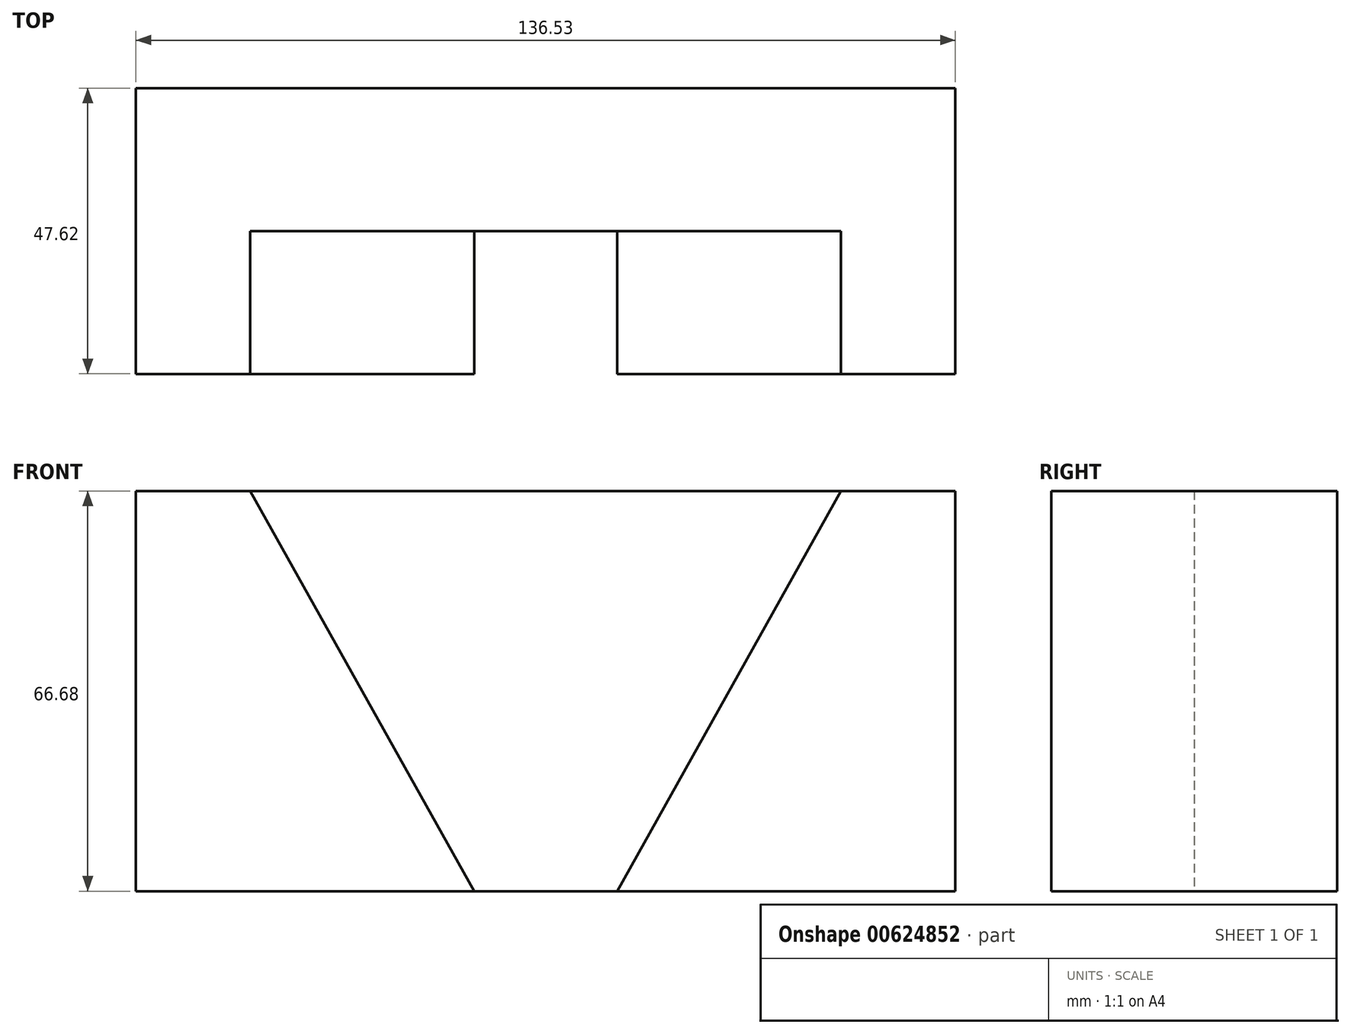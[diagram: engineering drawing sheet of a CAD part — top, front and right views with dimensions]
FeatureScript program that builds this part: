
annotation { "Feature Type Name" : "Feature", "Feature Type Description" : "" }
export const myFeature = defineFeature(function(context is Context, id is Id, definition is map)
    precondition{}
    {
        {
            var Q0;
            Q0=qCreatedBy(makeId("Front.planeOp"),FACE);
            var sketch = newSketch(context, id + "F0", { "sketchPlane" : qUnion([Q0])});
            skLineSegment(sketch, "E0.bottom", {"start": v(17.22, 0) * mm, "end": v(-119.3, 0) * mm});
            skLineSegment(sketch, "E0.top", {"start": v(17.22, 66.68) * mm, "end": v(-119.3, 66.67) * mm});
            skLineSegment(sketch, "E0.left", {"start": v(17.22, 0) * mm, "end": v(17.22, 66.68) * mm});
            skLineSegment(sketch, "E0.right", {"start": v(-119.3, 0) * mm, "end": v(-119.3, 66.68) * mm});
            skPoint(sketch, "E0.middle", {"position": v(-51.05, 33.34) * mm});
            skSolve(sketch);
        }
        {
            var Q0;
            Q0=makeQuery(id+"F0.imprint","IMPRINT",FACE,{"disambiguationData":[TD([[makeQuery(id+"F0.imprint","IMPRINT",EDGE,{"derivedFrom":sQuery(id+"F0.wireOp",EDGE,"E0.bottom")}),-1.0]])]});
            extrude(context, id + "F1", {"entities" : qUnion([Q0]), "depth" : 47.62 * mm, "offsetDistance" : 25.4 * mm});
        }
        {
            var Q0;
            Q0=makeQuery(id+"F1.opExtrude","CAP_FACE",FACE,{"disambiguationData":[OSD([sQuery(id+"F0.wireOp",EDGE,"E0.bottom"),sQuery(id+"F0.wireOp",EDGE,"E0.top"),sQuery(id+"F0.wireOp",EDGE,"E0.left"),sQuery(id+"F0.wireOp",EDGE,"E0.right")])],"isStart":false});
            var sketch = newSketch(context, id + "F2", { "sketchPlane" : qUnion([Q0])});
            skLineSegment(sketch, "E1", {"start": v(-100.26, 66.68) * mm, "end": v(-62.95, 0) * mm});
            skLineSegment(sketch, "E2", {"start": v(-1.83, 66.68) * mm, "end": v(-39.14, 0) * mm});
            skSolve(sketch);
        }
        {
            var Q0;
            Q0 = qSketchRegion(id + "F2", true);
            var Q1;
            {var subQ0=sQuery(id+"F2.wireOp",EDGE,"E1");Q1=makeQuery(id+"F2.imprint","IMPRINT",FACE,{"disambiguationData":[TD([[makeQuery(id+"F2.imprint","IMPRINT",EDGE,{"derivedFrom":subQ0}),1.0]])]});}
            extrude(context, id + "F3", {"entities" : qUnion([Q0, Q1]), "operationType" : NewBodyOperationType.REMOVE, "oppositeDirection" : true, "depth" : 23.8 * mm, "offsetDistance" : 25.4 * mm});
        }
    });
